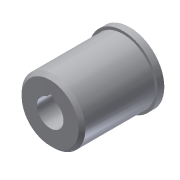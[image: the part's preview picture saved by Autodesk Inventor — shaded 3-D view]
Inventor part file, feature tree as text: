
AUTODESK INVENTOR PART (.ipt)
format: ipt  version: 2013 (Build 170138000, 138)  size: 104,448 bytes
history: native  units: in
note: dims shown in document units (in); Inventor stores cm internally (conversion verified against a paired STEP export)
features: extrude x3, sketch x3, chamfer x1
ambient origin geometry x8: Origin, YZ Plane, XZ Plane, XY Plane, X Axis, Y Axis, Z Axis, Center Point
bodies: Solid1 (feature_tree)
feature tree (7):
  extrude  "Extrusion1"  Depth=1.375in TaperAngle=0.0deg
  extrude  "Extrusion2"  Depth=0.125in TaperAngle=0.0deg
  extrude  "Extrusion3"  Depth=0.125in
  chamfer  "Chamfer1"  Distance=0.125in
  sketch  "Sketch1"  dims[d0=1.2in d2=1.375in d3=0.0in]
  sketch  "Sketch2"  dims[d5=1.3in d6=0.125in d7=0.0in]
  sketch  "Sketch3"  dims[d8=0.5in d9=0.125in d10=0.125in d11=0.125in d12=0.0in d13=0.0625in d14=0.125in d15=45.0deg]
